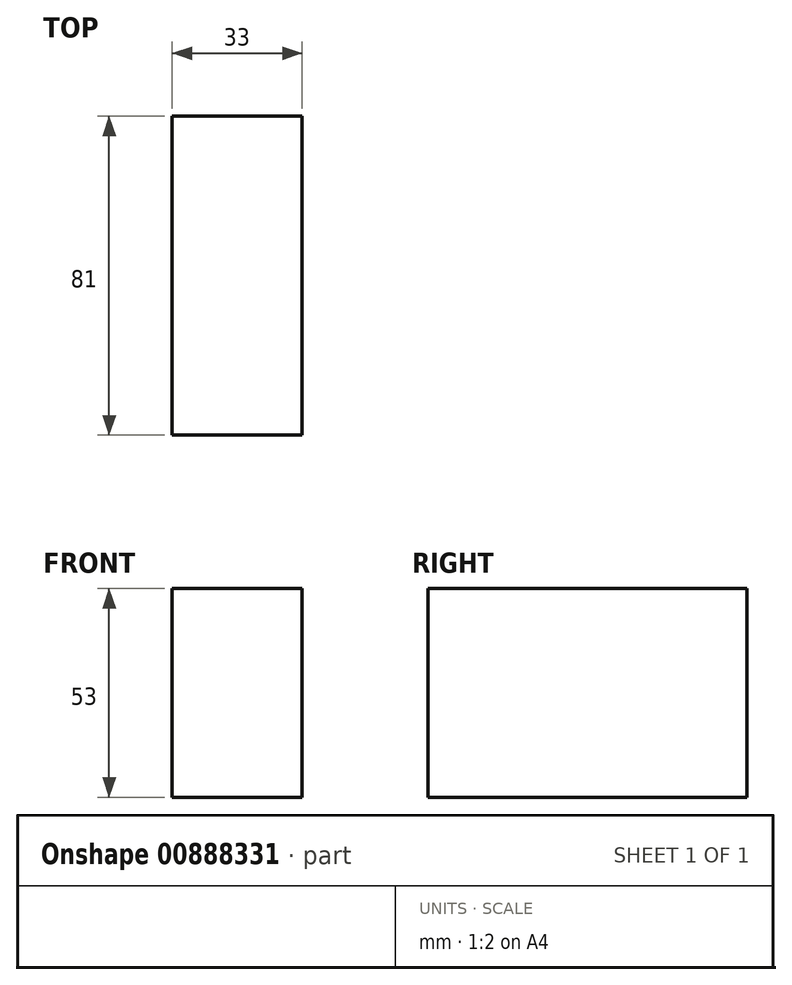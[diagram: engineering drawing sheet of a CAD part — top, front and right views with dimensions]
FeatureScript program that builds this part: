
annotation { "Feature Type Name" : "Feature", "Feature Type Description" : "" }
export const myFeature = defineFeature(function(context is Context, id is Id, definition is map)
    precondition{}
    {
        {
            var Q0;
            Q0=qCreatedBy(makeId("Top.planeOp"),FACE);
            var sketch = newSketch(context, id + "F0", { "sketchPlane" : qUnion([Q0])});
            skLineSegment(sketch, "E0.bottom", {"start": v(-16.5, 40.5) * mm, "end": v(16.5, 40.5) * mm});
            skLineSegment(sketch, "E0.top", {"start": v(-16.5, -40.5) * mm, "end": v(16.5, -40.5) * mm});
            skLineSegment(sketch, "E0.left", {"start": v(-16.5, 40.5) * mm, "end": v(-16.5, -40.5) * mm});
            skLineSegment(sketch, "E0.right", {"start": v(16.5, 40.5) * mm, "end": v(16.5, -40.5) * mm});
            skPoint(sketch, "E0.middle", {"position": v(0, 0) * mm});
            skSolve(sketch);
        }
        {
            var Q0;
            Q0=makeQuery(id+"F0.imprint","IMPRINT",FACE,{"disambiguationData":[TD([[makeQuery(id+"F0.imprint","IMPRINT",EDGE,{"derivedFrom":sQuery(id+"F0.wireOp",EDGE,"E0.bottom")}),-1.0]])]});
            extrude(context, id + "F1", {"entities" : qUnion([Q0]), "depth" : 53 * mm, "offsetDistance" : 25 * mm});
        }
    });
